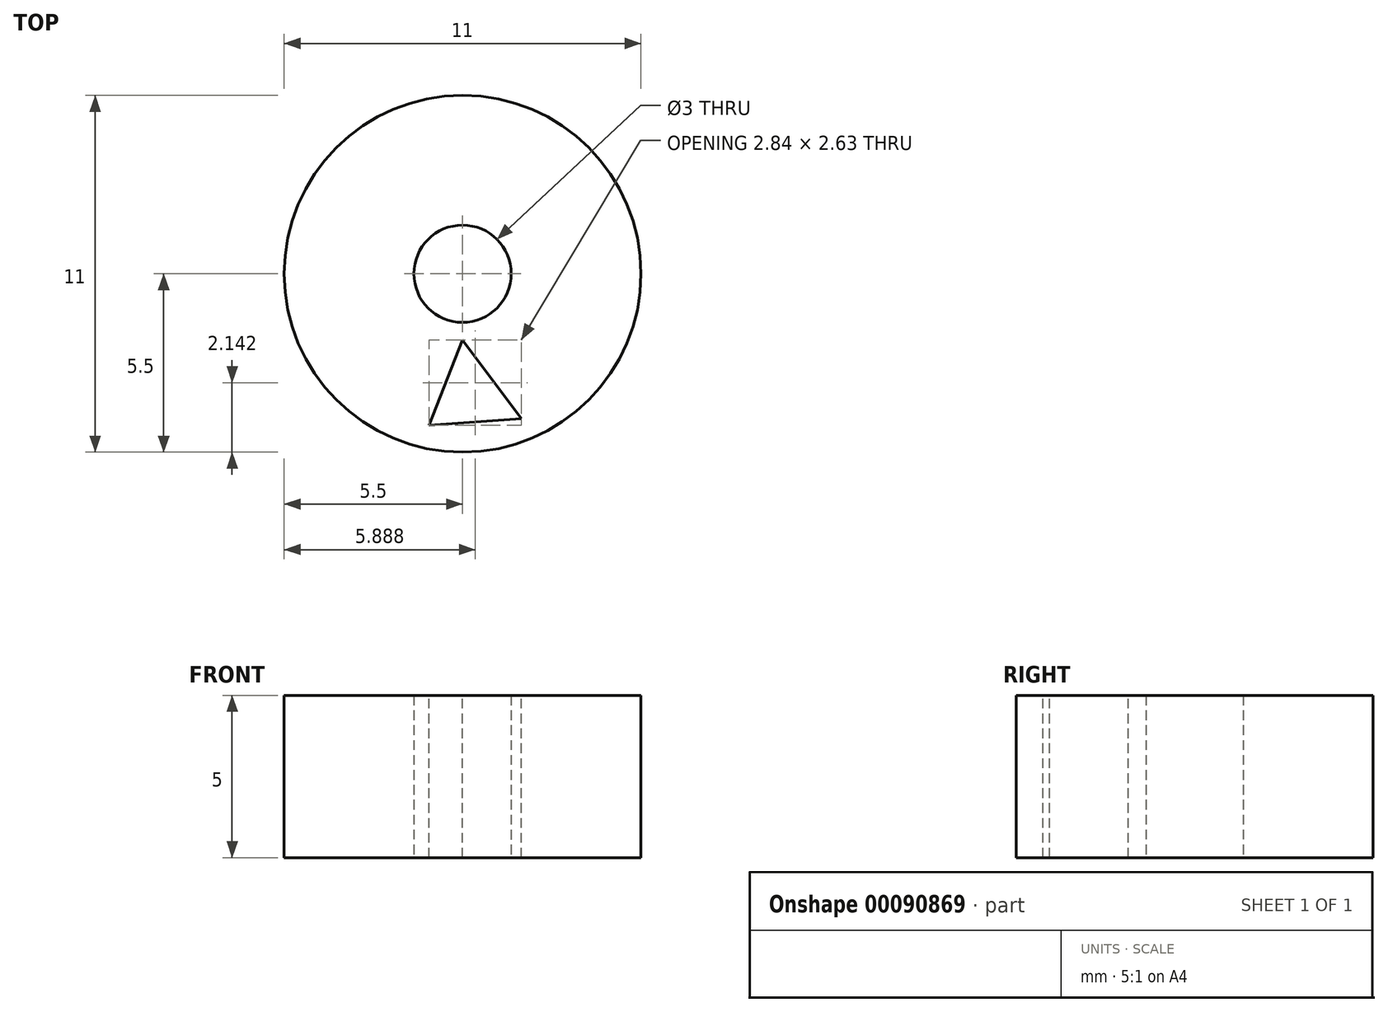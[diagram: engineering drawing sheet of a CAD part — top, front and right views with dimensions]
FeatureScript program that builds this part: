
annotation { "Feature Type Name" : "Feature", "Feature Type Description" : "" }
export const myFeature = defineFeature(function(context is Context, id is Id, definition is map)
    precondition{}
    {
        {
            var Q0;
            Q0=qCreatedBy(makeId("Top.planeOp"),FACE);
            var sketch = newSketch(context, id + "F0", { "sketchPlane" : qUnion([Q0])});
            skCircle(sketch, "E0", {"center": v(0, 0) * mm, "radius": 5.5 * mm});
            skCircle(sketch, "E1", {"center": v(0, 0) * mm, "radius": 1.5 * mm});
            skSolve(sketch);
        }
        {
            var Q0;
            Q0 = qSketchRegion(id + "F0", true);
            extrude(context, id + "F1", {"entities" : qUnion([Q0]), "depth" : 5 * mm});
        }
        {
            var Q0;
            Q0=makeQuery(id+"F1.opExtrude","CAP_FACE",FACE,{"disambiguationData":[OSD([sQuery(id+"F0.wireOp",EDGE,"E0"),sQuery(id+"F0.wireOp",EDGE,"E1")])],"isStart":false});
            var sketch = newSketch(context, id + "F2", { "sketchPlane" : qUnion([Q0])});
            skPoint(sketch, "E2.middle", {"position": v(0, 0) * mm});
            skLineSegment(sketch, "E3", {"start": v(0, -2.04) * mm, "end": v(-1.03, -4.67) * mm});
            skLineSegment(sketch, "E4", {"start": v(-1.03, -4.67) * mm, "end": v(1.8, -4.46) * mm});
            skLineSegment(sketch, "E5", {"start": v(1.8, -4.46) * mm, "end": v(0, -2.04) * mm});
            skSolve(sketch);
        }
        {
            var Q0;
            Q0=makeQuery(id+"F2.imprint","IMPRINT",FACE,{"disambiguationData":[TD([[makeQuery(id+"F2.imprint","IMPRINT",EDGE,{"derivedFrom":sQuery(id+"F2.wireOp",EDGE,"E3")}),1.0]])]});
            extrude(context, id + "F3", {"entities" : qUnion([Q0]), "operationType" : NewBodyOperationType.REMOVE, "oppositeDirection" : true, "depth" : 5 * mm});
        }
    });
